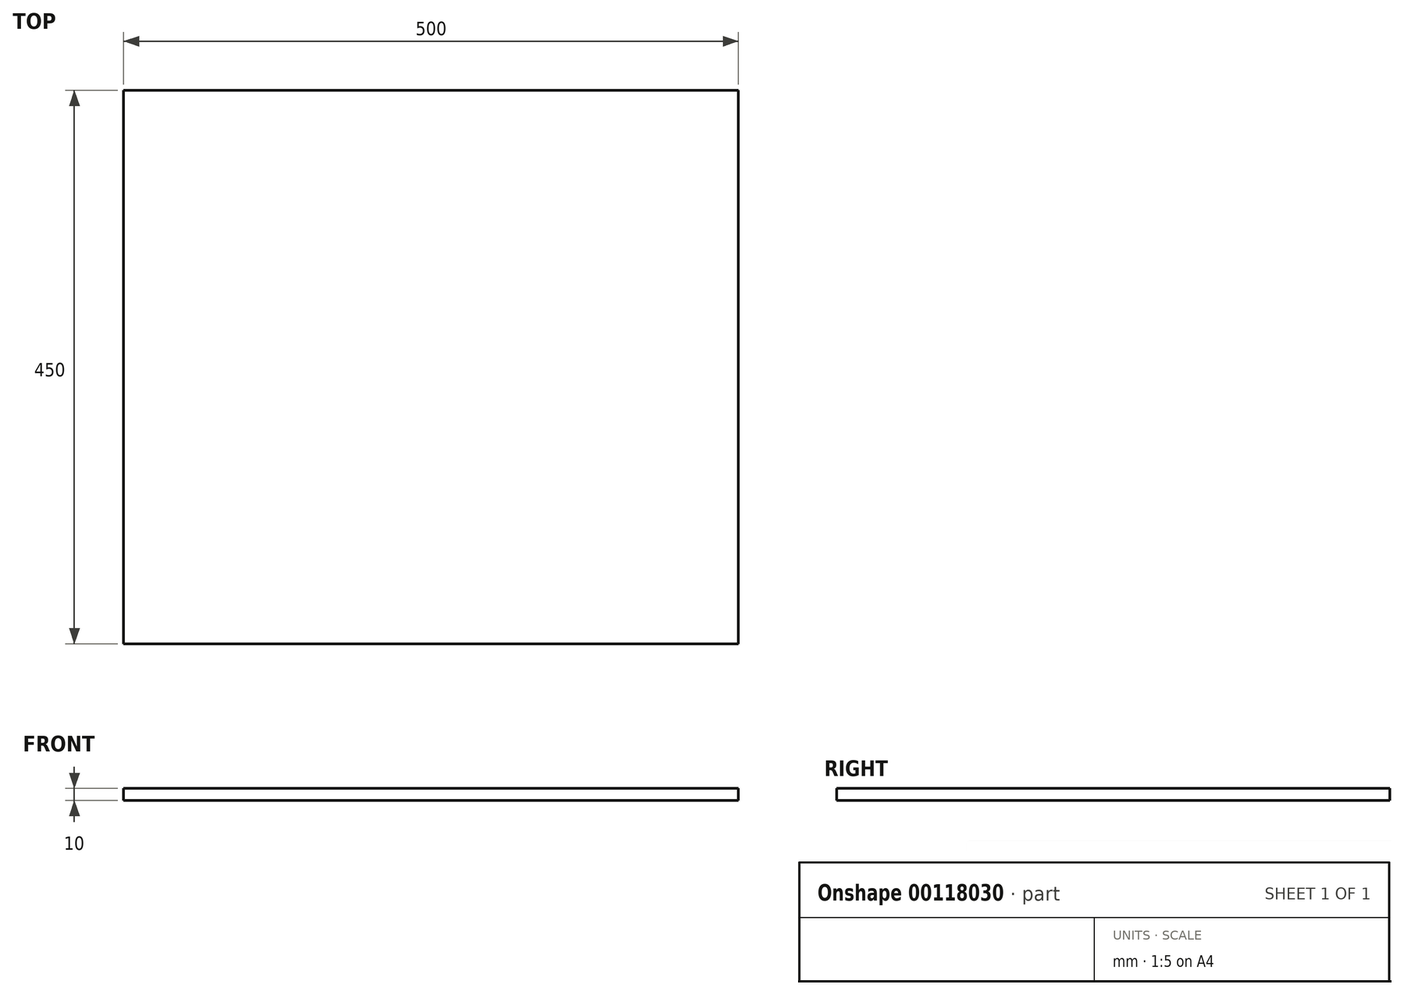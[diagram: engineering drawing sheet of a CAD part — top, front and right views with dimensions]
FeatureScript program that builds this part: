
annotation { "Feature Type Name" : "Feature", "Feature Type Description" : "" }
export const myFeature = defineFeature(function(context is Context, id is Id, definition is map)
    precondition{}
    {
        {
            var Q0;
            Q0=qCreatedBy(makeId("Top.planeOp"),FACE);
            var sketch = newSketch(context, id + "F0", { "sketchPlane" : qUnion([Q0])});
            skLineSegment(sketch, "E0.bottom", {"start": v(-249.15, 237.68) * mm, "end": v(250.85, 237.68) * mm});
            skLineSegment(sketch, "E0.top", {"start": v(-249.15, -212.32) * mm, "end": v(250.85, -212.32) * mm});
            skLineSegment(sketch, "E0.left", {"start": v(-249.15, 237.68) * mm, "end": v(-249.15, -212.32) * mm});
            skLineSegment(sketch, "E0.right", {"start": v(250.85, 237.68) * mm, "end": v(250.85, -212.32) * mm});
            skSolve(sketch);
        }
        {
            var Q0;
            Q0=makeQuery(id+"F0.imprint","IMPRINT",FACE,{"disambiguationData":[TD([[makeQuery(id+"F0.imprint","IMPRINT",EDGE,{"derivedFrom":sQuery(id+"F0.wireOp",EDGE,"E0.bottom")}),-1.0]])]});
            extrude(context, id + "F1", {"entities" : qUnion([Q0]), "depth" : 10 * mm});
        }
    });
